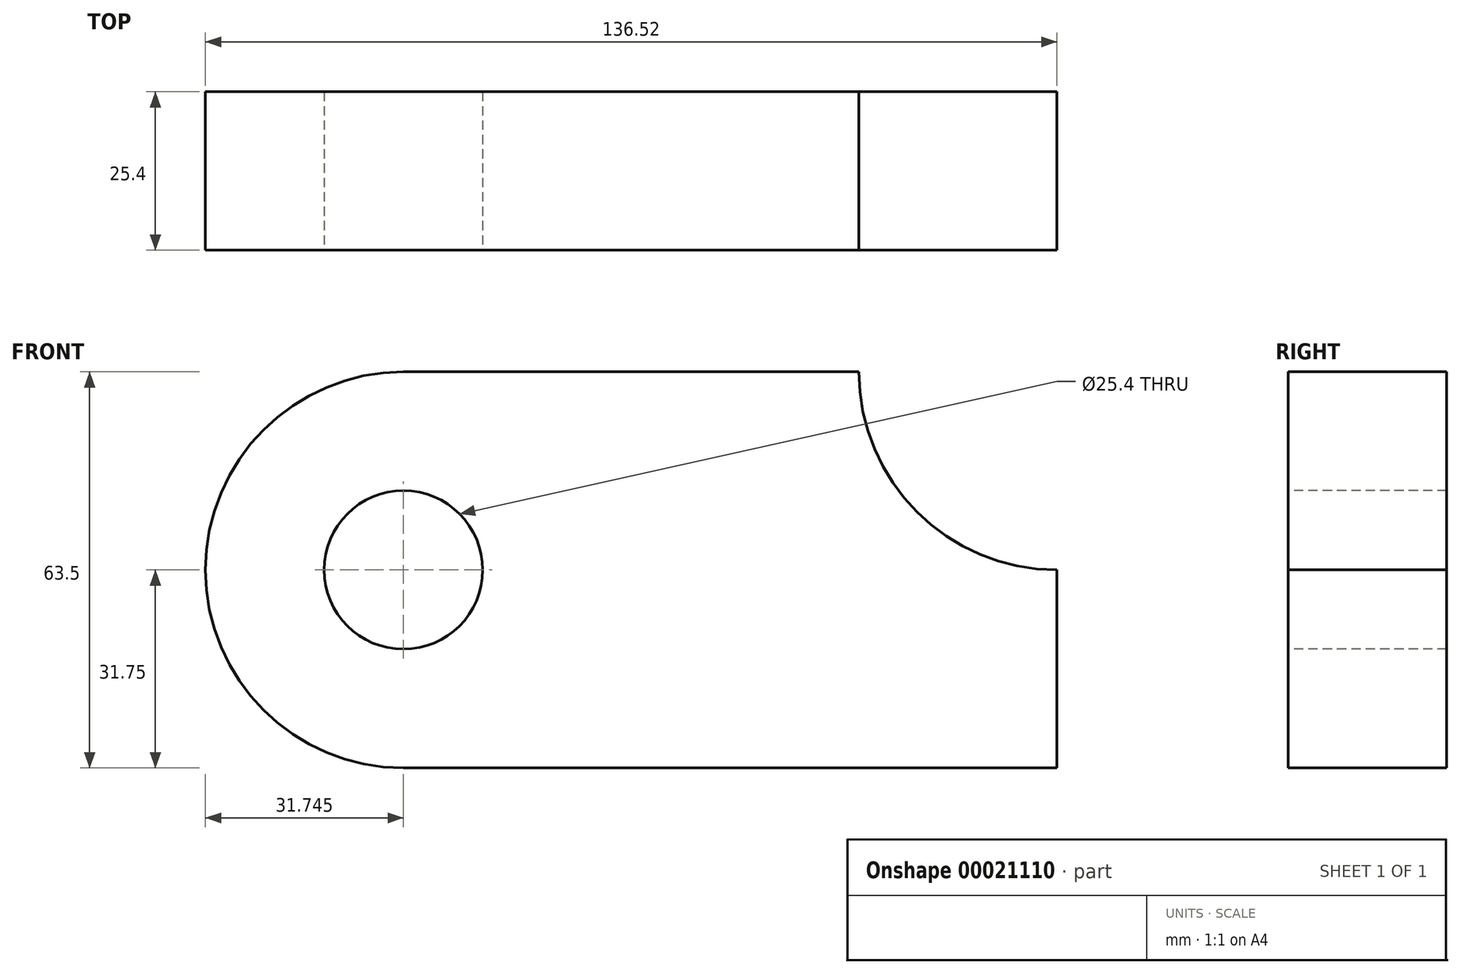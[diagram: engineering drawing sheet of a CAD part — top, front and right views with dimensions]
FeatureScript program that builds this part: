
annotation { "Feature Type Name" : "Feature", "Feature Type Description" : "" }
export const myFeature = defineFeature(function(context is Context, id is Id, definition is map)
    precondition{}
    {
        {
            var Q0;
            Q0=qCreatedBy(makeId("Front.planeOp"),FACE);
            var sketch = newSketch(context, id + "F0", { "sketchPlane" : qUnion([Q0])});
            skLineSegment(sketch, "E0.bottom", {"start": v(0, 0) * mm, "end": v(-104.78, 0) * mm});
            skLineSegment(sketch, "E0.top", {"start": v(0, 63.5) * mm, "end": v(-104.78, 63.5) * mm});
            skLineSegment(sketch, "E0.left", {"start": v(0, 0) * mm, "end": v(0, 63.5) * mm});
            skLineSegment(sketch, "E0.right", {"start": v(-104.78, 0) * mm, "end": v(-104.78, 63.5) * mm});
            skCircle(sketch, "E1", {"center": v(-104.78, 31.75) * mm, "radius": 31.75 * mm});
            skCircle(sketch, "E2", {"center": v(-104.78, 31.75) * mm, "radius": 12.7 * mm});
            skCircle(sketch, "E3", {"center": v(0, 63.5) * mm, "radius": 31.75 * mm});
            skSolve(sketch);
        }
        {
            var Q0;
            {var subQ4=sQuery(id+"F0.wireOp",EDGE,"E0.bottom");Q0=makeQuery(id+"F0.imprint","IMPRINT",FACE,{"disambiguationData":[TD([[makeQuery(id+"F0.imprint","IMPRINT",EDGE,{"derivedFrom":subQ4}),-1.0]])]});}
            var Q1;
            {var subQ0=sQuery(id+"F0.wireOp",EDGE,"E2");var subQ1=sQuery(id+"F0.wireOp",EDGE,"E0.right");var subQ3=makeQuery(id+"F0.imprint","INTERSECT",VERTEX,{"disambiguationData":[OD(0.0)],"derivedFrom":[subQ1,subQ0]});Q1=makeQuery(id+"F0.imprint","IMPRINT",FACE,{"disambiguationData":[TD([[makeQuery(id+"F0.imprint","IMPRINT",EDGE,{"disambiguationData":[TD([[subQ3,1.0]])],"derivedFrom":subQ0}),-1.0]])]});}
            var Q2;
            {var subQ0=sQuery(id+"F0.wireOp",EDGE,"E2");var subQ1=sQuery(id+"F0.wireOp",EDGE,"E0.right");var subQ3=makeQuery(id+"F0.imprint","INTERSECT",VERTEX,{"disambiguationData":[OD(0.0)],"derivedFrom":[subQ1,subQ0]});Q2=makeQuery(id+"F0.imprint","IMPRINT",FACE,{"disambiguationData":[TD([[makeQuery(id+"F0.imprint","IMPRINT",EDGE,{"disambiguationData":[TD([[subQ3,-1.0]])],"derivedFrom":subQ0}),-1.0]])]});}
            extrude(context, id + "F1", {"entities" : qUnion([Q0, Q1, Q2]), "oppositeDirection" : true, "depth" : 25.4 * mm});
        }
    });
